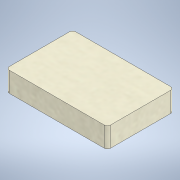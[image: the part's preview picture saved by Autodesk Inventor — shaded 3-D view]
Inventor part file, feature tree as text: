
AUTODESK INVENTOR PART (.ipt)
format: ipt  version: 2021 (Build 250183000, 183)  size: 112,128 bytes
history: native  units: mm
features: extrude x1, sketch x1
ambient origin geometry x8: Origin, YZ Plane, XZ Plane, XY Plane, X Axis, Y Axis, Z Axis, Center Point
bodies: Solid1 (feature_tree)
feature tree (2):
  extrude  "Extrusion1"  Depth=42.0mm
  sketch  "Sketch1"  dims[d0=64.0mm d1=42.0mm d2=2.0mm d3=12.7mm d4=0.0mm]
